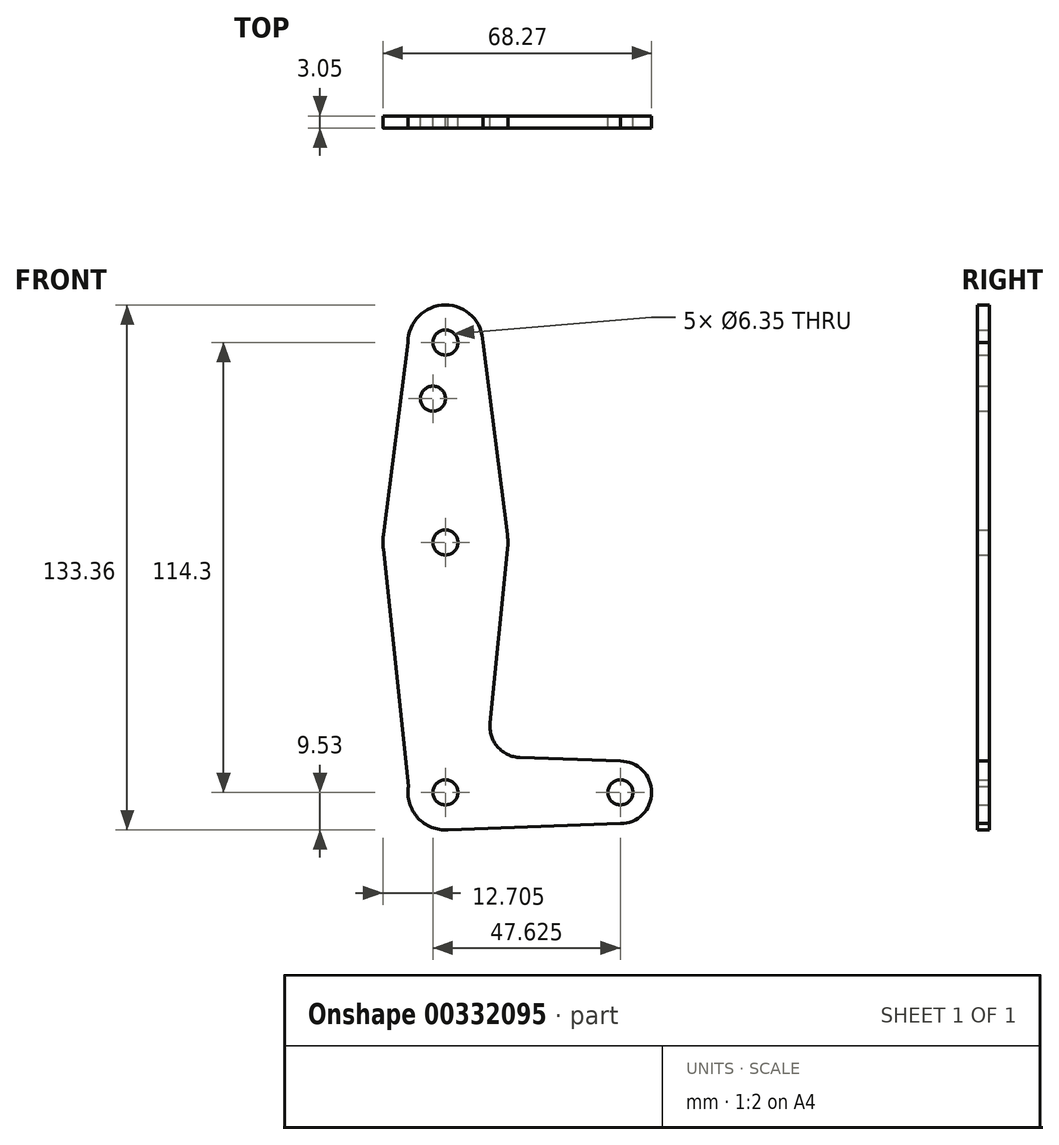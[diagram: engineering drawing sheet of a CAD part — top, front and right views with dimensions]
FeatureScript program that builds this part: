
annotation { "Feature Type Name" : "Feature", "Feature Type Description" : "" }
export const myFeature = defineFeature(function(context is Context, id is Id, definition is map)
    precondition{}
    {
        {
            var Q0;
            Q0=qCreatedBy(makeId("Front.planeOp"),FACE);
            var sketch = newSketch(context, id + "F0", { "sketchPlane" : qUnion([Q0])});
            skLineSegment(sketch, "E0", {"start": v(0, 0) * mm, "end": v(0, 114.3) * mm, "construction": true});
            skPoint(sketch, "E1.end.orphan", {"position": v(37.76, 0) * mm});
            skPoint(sketch, "E1.start.orphan", {"position": v(0, -1.48) * mm});
            skLineSegment(sketch, "E2", {"start": v(0, 0) * mm, "end": v(44.45, 0) * mm, "construction": true});
            skCircle(sketch, "E3", {"center": v(44.45, 0) * mm, "radius": 7.94 * mm});
            skCircle(sketch, "E4", {"center": v(0, 0) * mm, "radius": 9.53 * mm});
            skCircle(sketch, "E5", {"center": v(0, 63.5) * mm, "radius": 15.88 * mm});
            skCircle(sketch, "E6", {"center": v(0, 114.3) * mm, "radius": 9.53 * mm});
            skLineSegment(sketch, "E7", {"start": v(0, 63.5) * mm, "end": v(0, 0) * mm, "construction": true});
            skLineSegment(sketch, "E8", {"start": v(9.53, 114.3) * mm, "end": v(15.75, 65.5) * mm});
            skLineSegment(sketch, "E9", {"start": v(-9.53, 114.3) * mm, "end": v(-15.75, 65.5) * mm});
            skPoint(sketch, "E10.start.orphan", {"position": v(15.79, 61.83) * mm});
            skPoint(sketch, "E11.end.orphan", {"position": v(-9.57, 0) * mm});
            skPoint(sketch, "E11.start.orphan", {"position": v(-15.79, 61.83) * mm});
            skLineSegment(sketch, "E12", {"start": v(-15.79, 61.83) * mm, "end": v(-8.87, -3.46) * mm});
            skLineSegment(sketch, "E13", {"start": v(15.79, 61.83) * mm, "end": v(11.34, 17.6) * mm});
            skLineSegment(sketch, "E14", {"start": v(44.45, 7.94) * mm, "end": v(18.97, 8.85) * mm});
            skLineSegment(sketch, "E15", {"start": v(44.45, -7.94) * mm, "end": v(0, -9.53) * mm});
            skCircle(sketch, "E16", {"center": v(0, 114.3) * mm, "radius": 3.18 * mm});
            skCircle(sketch, "E17", {"center": v(0, 63.5) * mm, "radius": 3.18 * mm});
            skCircle(sketch, "E18", {"center": v(0, 0) * mm, "radius": 3.18 * mm});
            skCircle(sketch, "E19", {"center": v(44.45, 0) * mm, "radius": 3.18 * mm});
            skCircle(sketch, "E20", {"center": v(-3.18, 100.03) * mm, "radius": 3.18 * mm});
            skPoint(sketch, "E21.newPointA", {"position": v(9.22, -3.46) * mm});
            skPoint(sketch, "E21.newPointB", {"position": v(0, 9.53) * mm});
            skArc(sketch, "E21.filletArc", {"start": v(11.34, 17.6) * mm, "mid": v(13.26, 11.57) * mm, "end": v(18.97, 8.85) * mm});
            skSolve(sketch);
        }
        {
            var Q0;
            Q0 = qSketchRegion(id + "F0", true);
            extrude(context, id + "F1", {"entities" : qUnion([Q0]), "depth" : 3.05 * mm});
        }
    });
